# Revit family: Door_SS_The Sliding Door Company_Wall Slide to Column_2-Panel Double Track (Top Mount)
name_source: partatom
category: Doors
units: mm (PartAtom-declared; Revit-internal decimal feet)

## family parameters
Always vertical = Yes
Cut with Voids When Loaded = No
Host = Wall
OmniClass Number = 23.30.10.00
OmniClass Title = Doors
Room Calculation Point = No
Shared = No

## types (1)
- Suspended Wall Slide to Column 2-Panel & Track (Top Mounted)
    ADA Opening Clearance = Minimum of 32 inches Opening Clearance
    Analytic Construction = <None>
    Description = Suspended Wall Slide to Column 2-Panel & Track (Top Mounted)
    Function = Interior
    Height = 96"
    Manufacturer = The Sliding Door Company
    Maximum Order Height = 108 inches
    Maximum Order Width = 99.5 inches
    Model = Suspended Wall Slide to Column 2-Panel & Track (Top Mounted)
    Opening Clearance Height = 92 1/2"
    Opening Clearance Width = 77 1/2"
    Order Height = 96"
    Order Width = 80"
    Panel Height = 92 5/8"
    Panel Width = 41 1/4"
    Stile/Rail = 2 1/2"
    Suspended System Frame = Available only in 2.5 inches
    Thickness = 1 1/4"
    Track Length = 118 3/4"
    URL = https://www.slidingdoorco.com
    Wall Closure = By host
    Width = 80"
    With Column = Yes
    Without Column = No

## geometry (parser evidence)
native form markers: Blend x2, Sweep x8
no freeform markers — native parametric forms only
